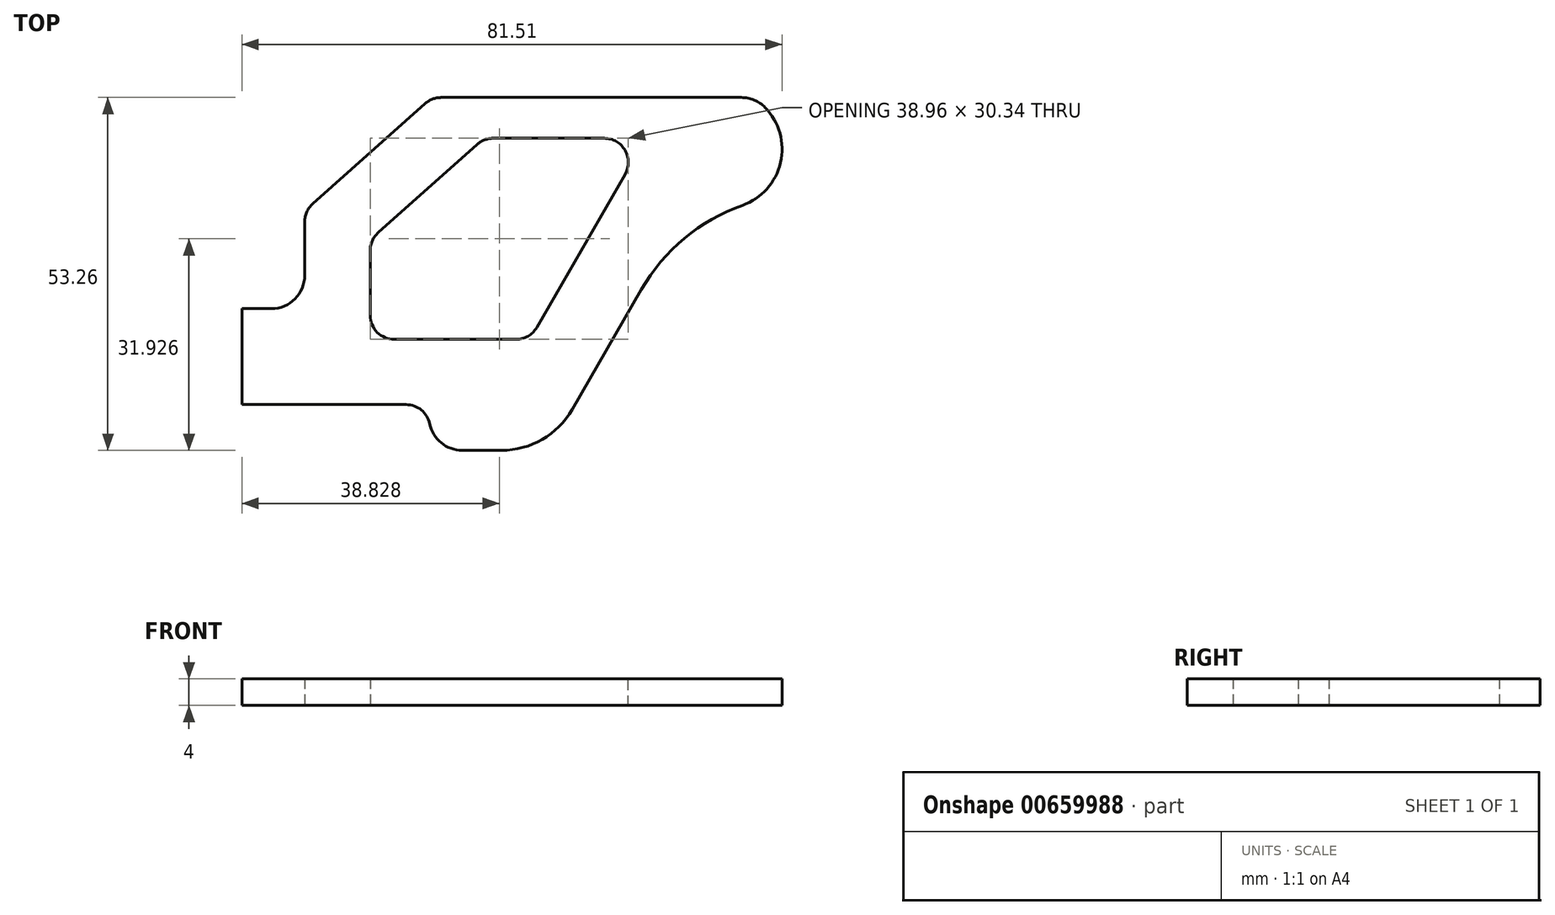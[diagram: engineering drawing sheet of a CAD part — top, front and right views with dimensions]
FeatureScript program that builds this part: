
annotation { "Feature Type Name" : "Feature", "Feature Type Description" : "" }
export const myFeature = defineFeature(function(context is Context, id is Id, definition is map)
    precondition{}
    {
        {
            var Q0;
            Q0=qCreatedBy(makeId("Top.planeOp"),FACE);
            var sketch = newSketch(context, id + "F0", { "sketchPlane" : qUnion([Q0])});
            skLineSegment(sketch, "E0", {"start": v(0, 0) * mm, "end": v(0, -14.5) * mm});
            skLineSegment(sketch, "E1", {"start": v(0, -14.5) * mm, "end": v(28.4, -14.5) * mm});
            skLineSegment(sketch, "E2", {"start": v(28.4, -14.5) * mm, "end": v(28.4, -21.4) * mm});
            skLineSegment(sketch, "E3", {"start": v(46.27, -21.4) * mm, "end": v(77.01, 31.86) * mm});
            skLineSegment(sketch, "E4", {"start": v(28.67, 31.86) * mm, "end": v(9.46, 14.74) * mm});
            skLineSegment(sketch, "E5", {"start": v(9.46, 14.74) * mm, "end": v(9.46, 0) * mm});
            skLineSegment(sketch, "E6", {"start": v(9.46, 0) * mm, "end": v(0, 0) * mm});
            skLineSegment(sketch, "E7", {"start": v(19.35, 10.4) * mm, "end": v(36.52, 25.7) * mm});
            skLineSegment(sketch, "E8", {"start": v(36.52, 25.7) * mm, "end": v(60.96, 25.7) * mm});
            skLineSegment(sketch, "E9", {"start": v(60.96, 25.7) * mm, "end": v(43.44, -4.65) * mm});
            skLineSegment(sketch, "E10", {"start": v(43.44, -4.65) * mm, "end": v(19.35, -4.65) * mm});
            skLineSegment(sketch, "E11", {"start": v(19.35, -4.65) * mm, "end": v(19.35, 10.4) * mm});
            skLineSegment(sketch, "E12", {"start": v(28.4, -21.4) * mm, "end": v(46.27, -21.4) * mm});
            skLineSegment(sketch, "E13", {"start": v(28.67, 31.86) * mm, "end": v(77.01, 31.86) * mm});
            skArc(sketch, "E14", {"start": v(68.01, 16.27) * mm, "mid": v(80.3, 19.56) * mm, "end": v(77.01, 31.86) * mm});
            skSolve(sketch);
        }
        {
            var Q0;
            Q0 = qSketchRegion(id + "F0", true);
            extrude(context, id + "F1", {"entities" : qUnion([Q0]), "depth" : 4 * mm, "offsetDistance" : 25 * mm});
        }
        {
            var Q0;
            Q0=makeQuery(id+"F1.opExtrude","SWEPT_EDGE",EDGE,{"disambiguationData":[OSD([sQuery(id+"F0.wireOp",EDGE,"E4"),sQuery(id+"F0.wireOp",EDGE,"E5")])]});
            var Q1;
            Q1=makeQuery(id+"F1.opExtrude","SWEPT_EDGE",EDGE,{"disambiguationData":[OSD([sQuery(id+"F0.wireOp",EDGE,"E4"),sQuery(id+"F0.wireOp",EDGE,"E13")])]});
            var Q2;
            Q2=makeQuery(id+"F1.opExtrude","SWEPT_EDGE",EDGE,{"disambiguationData":[OSD([sQuery(id+"F0.wireOp",EDGE,"E10"),sQuery(id+"F0.wireOp",EDGE,"E11")])]});
            var Q3;
            Q3=makeQuery(id+"F1.opExtrude","SWEPT_EDGE",EDGE,{"disambiguationData":[OSD([sQuery(id+"F0.wireOp",EDGE,"E7"),sQuery(id+"F0.wireOp",EDGE,"E11")])]});
            var Q4;
            Q4=makeQuery(id+"F1.opExtrude","SWEPT_EDGE",EDGE,{"disambiguationData":[OSD([sQuery(id+"F0.wireOp",EDGE,"E7"),sQuery(id+"F0.wireOp",EDGE,"E8")])]});
            var Q5;
            Q5=makeQuery(id+"F1.opExtrude","SWEPT_EDGE",EDGE,{"disambiguationData":[OSD([sQuery(id+"F0.wireOp",EDGE,"E8"),sQuery(id+"F0.wireOp",EDGE,"E9")])]});
            var Q6;
            Q6=makeQuery(id+"F1.opExtrude","SWEPT_EDGE",EDGE,{"disambiguationData":[OSD([sQuery(id+"F0.wireOp",EDGE,"E9"),sQuery(id+"F0.wireOp",EDGE,"E10")])]});
            var Q7;
            Q7=makeQuery(id+"F1.opExtrude","SWEPT_EDGE",EDGE,{"disambiguationData":[OSD([sQuery(id+"F0.wireOp",EDGE,"E1"),sQuery(id+"F0.wireOp",EDGE,"E2")])]});
            fillet(context, id + "F2", {"entities" : qUnion([Q0, Q1, Q2, Q3, Q4, Q5, Q6, Q7]), "radius" : 3.62 * mm, "tangentPropagation" : true, "allowEdgeOverflow" : false});
        }
        {
            var Q0;
            Q0=makeQuery(id+"F1.opExtrude","SWEPT_EDGE",EDGE,{"disambiguationData":[OSD([sQuery(id+"F0.wireOp",EDGE,"E5"),sQuery(id+"F0.wireOp",EDGE,"E6")])]});
            fillet(context, id + "F3", {"entities" : qUnion([Q0]), "radius" : 5 * mm, "tangentPropagation" : true, "allowEdgeOverflow" : false});
        }
        {
            var Q0;
            Q0=makeQuery(id+"F1.opExtrude","SWEPT_EDGE",EDGE,{"disambiguationData":[OSD([sQuery(id+"F0.wireOp",EDGE,"E3"),sQuery(id+"F0.wireOp",EDGE,"E14")])]});
            fillet(context, id + "F4", {"entities" : qUnion([Q0]), "radius" : 28.73 * mm, "tangentPropagation" : true, "allowEdgeOverflow" : false});
        }
        {
            var Q0;
            Q0=makeQuery(id+"F1.opExtrude","SWEPT_EDGE",EDGE,{"disambiguationData":[OSD([sQuery(id+"F0.wireOp",EDGE,"E3"),sQuery(id+"F0.wireOp",EDGE,"E13"),sQuery(id+"F0.wireOp",EDGE,"E14")])]});
            fillet(context, id + "F5", {"entities" : qUnion([Q0]), "radius" : 5 * mm, "tangentPropagation" : true, "allowEdgeOverflow" : false});
        }
        {
            var Q0;
            Q0=makeQuery(id+"F1.opExtrude","SWEPT_EDGE",EDGE,{"disambiguationData":[OSD([sQuery(id+"F0.wireOp",EDGE,"E2"),sQuery(id+"F0.wireOp",EDGE,"E12")])]});
            fillet(context, id + "F6", {"entities" : qUnion([Q0]), "radius" : 5 * mm, "tangentPropagation" : true, "allowEdgeOverflow" : false});
        }
        {
            var Q0;
            Q0=makeQuery(id+"F1.opExtrude","SWEPT_EDGE",EDGE,{"disambiguationData":[OSD([sQuery(id+"F0.wireOp",EDGE,"E3"),sQuery(id+"F0.wireOp",EDGE,"E12")])]});
            fillet(context, id + "F7", {"entities" : qUnion([Q0]), "radius" : 12.28 * mm, "tangentPropagation" : true, "allowEdgeOverflow" : false});
        }
    });
